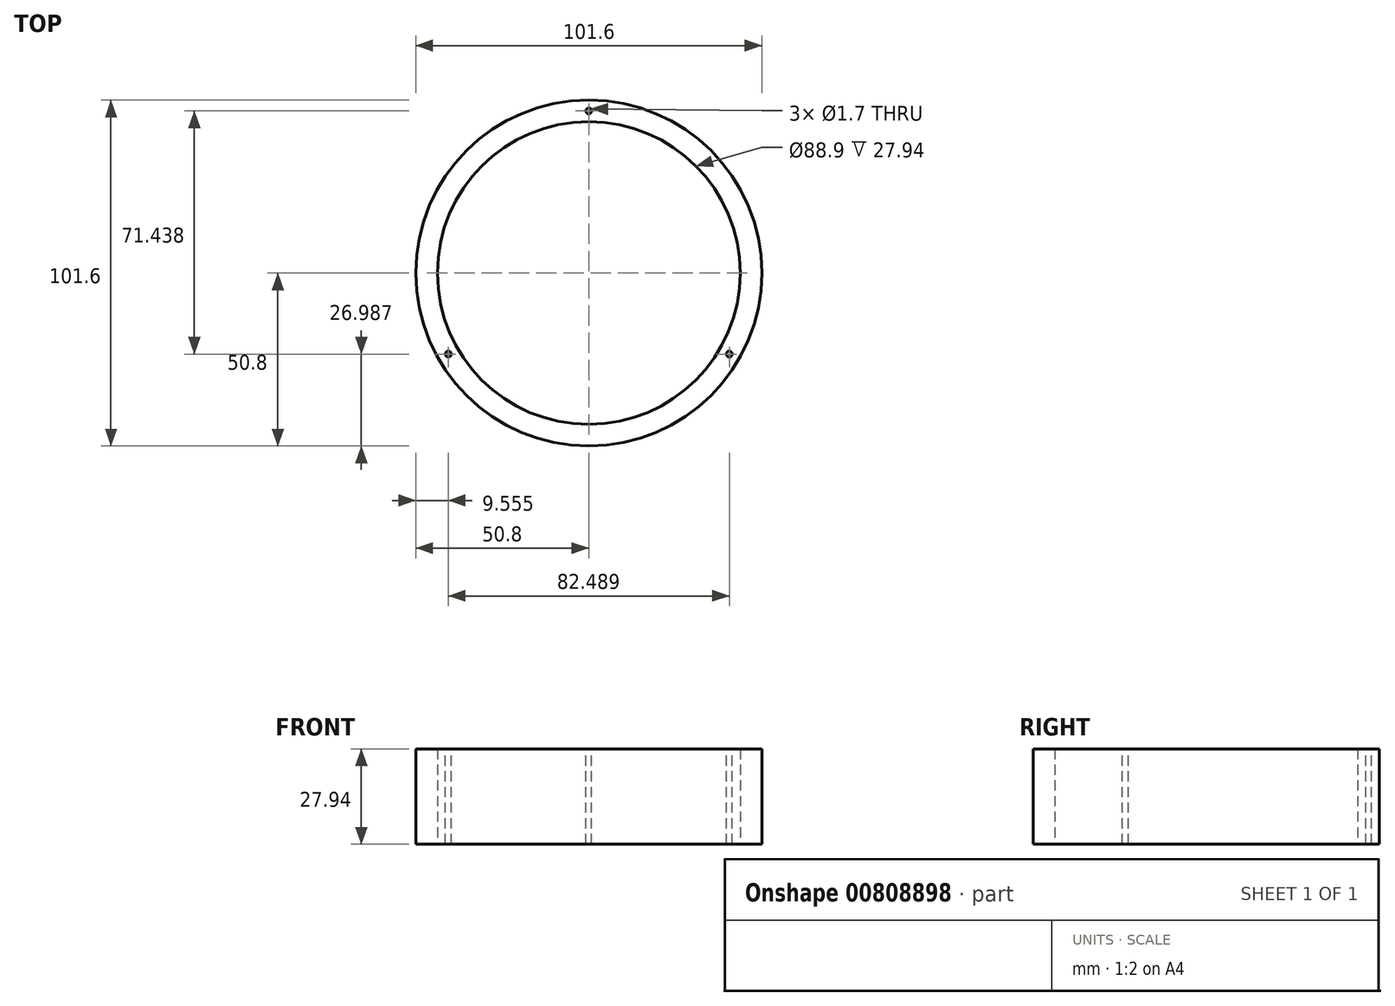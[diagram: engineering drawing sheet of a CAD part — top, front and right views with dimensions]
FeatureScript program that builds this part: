
annotation { "Feature Type Name" : "Feature", "Feature Type Description" : "" }
export const myFeature = defineFeature(function(context is Context, id is Id, definition is map)
    precondition{}
    {
        {
            var Q0;
            Q0=qCreatedBy(makeId("Top.planeOp"),FACE);
            var sketch = newSketch(context, id + "F0", { "sketchPlane" : qUnion([Q0])});
            skCircle(sketch, "E0", {"center": v(0, 0) * mm, "radius": 44.45 * mm});
            skCircle(sketch, "E1", {"center": v(0, 0) * mm, "radius": 50.8 * mm});
            skSolve(sketch);
        }
        {
            var Q0;
            Q0=makeQuery(id+"F0.imprint","IMPRINT",FACE,{"disambiguationData":[TD([[makeQuery(id+"F0.imprint","IMPRINT",EDGE,{"derivedFrom":sQuery(id+"F0.wireOp",EDGE,"E0")}),-1.0]])]});
            extrude(context, id + "F1", {"entities" : qUnion([Q0]), "flatOperationType" : FlatOperationType.REMOVE, "depth" : 27.94 * mm, "offsetDistance" : 25.4 * mm, "domain" : OperationDomain.MODEL});
        }
        {
            var Q0;
            Q0=makeQuery(id+"F1.opExtrude","CAP_FACE",FACE,{"disambiguationData":[OSD([sQuery(id+"F0.wireOp",EDGE,"E0"),sQuery(id+"F0.wireOp",EDGE,"E1"),sQuery(id+"F0.wireOp",EDGE,"Qu51MrwH-pxOF-z7DU-j5td-C3wyU67hcf0W"),sQuery(id+"F0.wireOp",EDGE,"e64d7bf3-b6c9-48f4-805c-10998a7faca8"),sQuery(id+"F0.wireOp",EDGE,"512e63a3-43d6-4e89-99d7-7b8725fe710e")])],"isStart":false});
            var sketch = newSketch(context, id + "F2", { "sketchPlane" : qUnion([Q0])});
            skPoint(sketch, "E2", {"position": v(41.24, -23.81) * mm});
            skLineSegment(sketch, "E3", {"start": v(0, 0) * mm, "end": v(43.37, -25.04) * mm});
            skLineSegment(sketch, "E4", {"start": v(0, 0) * mm, "end": v(-45.96, -26.53) * mm});
            skPoint(sketch, "E5", {"position": v(0, 47.62) * mm});
            skPoint(sketch, "E6", {"position": v(-41.24, -23.81) * mm});
            skSolve(sketch);
        }
        {
            var Q0;
            Q0=sQuery(id+"F2.wireOp",VERTEX,"E2");
            var Q1;
            Q1=makeQuery(id+"F1.opExtrude","SWEPT_BODY",BODY,{"disambiguationData":[OSD([sQuery(id+"F0.wireOp",EDGE,"E0"),sQuery(id+"F0.wireOp",EDGE,"E1")])]});
            hole(context, id + "F3", {"style" : HoleStyle.SIMPLE, "endStyle" : HoleEndStyle.BLIND, "holeDiameter" : 1.7 * mm, "majorDiameter" : 6.35 * mm, "holeDepth" : 27.94 * mm, "isTappedThrough" : true, "tappedDepth" : 12.7 * mm, "tapClearance" : 3, "startFromSketch" : true, "locations" : qUnion([Q0]), "scope" : qUnion([Q1])});
        }
        {
            var Q0;
            Q0=sQuery(id+"F2.wireOp",VERTEX,"E6");
            var Q1;
            Q1=sQuery(id+"F2.wireOp",VERTEX,"E5");
            var Q2;
            Q2=makeQuery(id+"F1.opExtrude","SWEPT_BODY",BODY,{"disambiguationData":[OSD([sQuery(id+"F0.wireOp",EDGE,"E0"),sQuery(id+"F0.wireOp",EDGE,"E1")])]});
            hole(context, id + "F4", {"style" : HoleStyle.SIMPLE, "endStyle" : HoleEndStyle.BLIND, "holeDiameter" : 1.7 * mm, "majorDiameter" : 6.35 * mm, "holeDepth" : 30.48 * mm, "isTappedThrough" : true, "tappedDepth" : 12.7 * mm, "tapClearance" : 3, "startFromSketch" : true, "locations" : qUnion([Q0, Q1]), "scope" : qUnion([Q2])});
        }
    });
